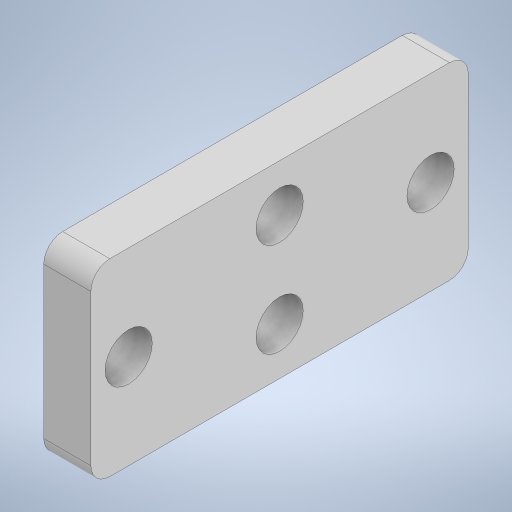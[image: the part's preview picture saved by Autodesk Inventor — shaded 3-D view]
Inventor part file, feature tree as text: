
AUTODESK INVENTOR PART (.ipt)
format: ipt  version: 2023 (Build 270158000, 158)  size: 221,696 bytes
history: native  units: mm
features: extrude x2, sketch x1, fillet x1
ambient origin geometry x8: Origin, YZ Plane, XZ Plane, XY Plane, X Axis, Y Axis, Z Axis, Center Point
bodies: Solido1 (feature_tree)
feature tree (4):
  sketch  "Schizzo1"
  extrude  "Estrusione1"  Depth=40.0mm
  fillet  "Raccordo1"  Radius=20.0mm
  extrude  "Estrusione2"  Depth=4.0mm
